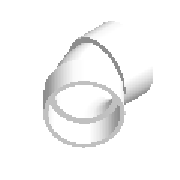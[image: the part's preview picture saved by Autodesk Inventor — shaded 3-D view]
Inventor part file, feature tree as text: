
AUTODESK INVENTOR PART (.ipt)
format: ipt  version: 2023.1 (Build 271208000, 208)  size: 223,232 bytes
history: native  units: mm (DEFAULTED — no unit token found)
features: other x6, sketch x4
ambient origin geometry x8: Origin, YZ Plane, XZ Plane, XY Plane, X Axis, Y Axis, Z Axis, Center Point
bodies: Solid1 (feature_tree)
feature tree (10):
  other  "Work Point1"
  other  "Work Point2"
  other  "Work Axis1"
  other  "Work Point3"
  other  "Work Axis2"
  other  "Work Point4"
  sketch  "Sketch1"  dims[d1=89.45mm]
  sketch  "Sketch2"  dims[d2=88.65mm]
  sketch  "Sketch3"  dims[d0=89.45mm]
  sketch  "Sketch4"  dims[d3=88.65mm d4=3.4mm d5=40.0mm d6=3.4mm d7=77.2mm d39=90.0deg d8=77.2mm d9=3.6mm d10=0.0mm d11=40.0mm d12=3.4mm d13=77.2mm d14=88.65mm d15=89.45mm d16=3.4mm d98=90.0deg d17=45.0deg d18=21.6mm d19=21.6mm d102=0.0mm]
